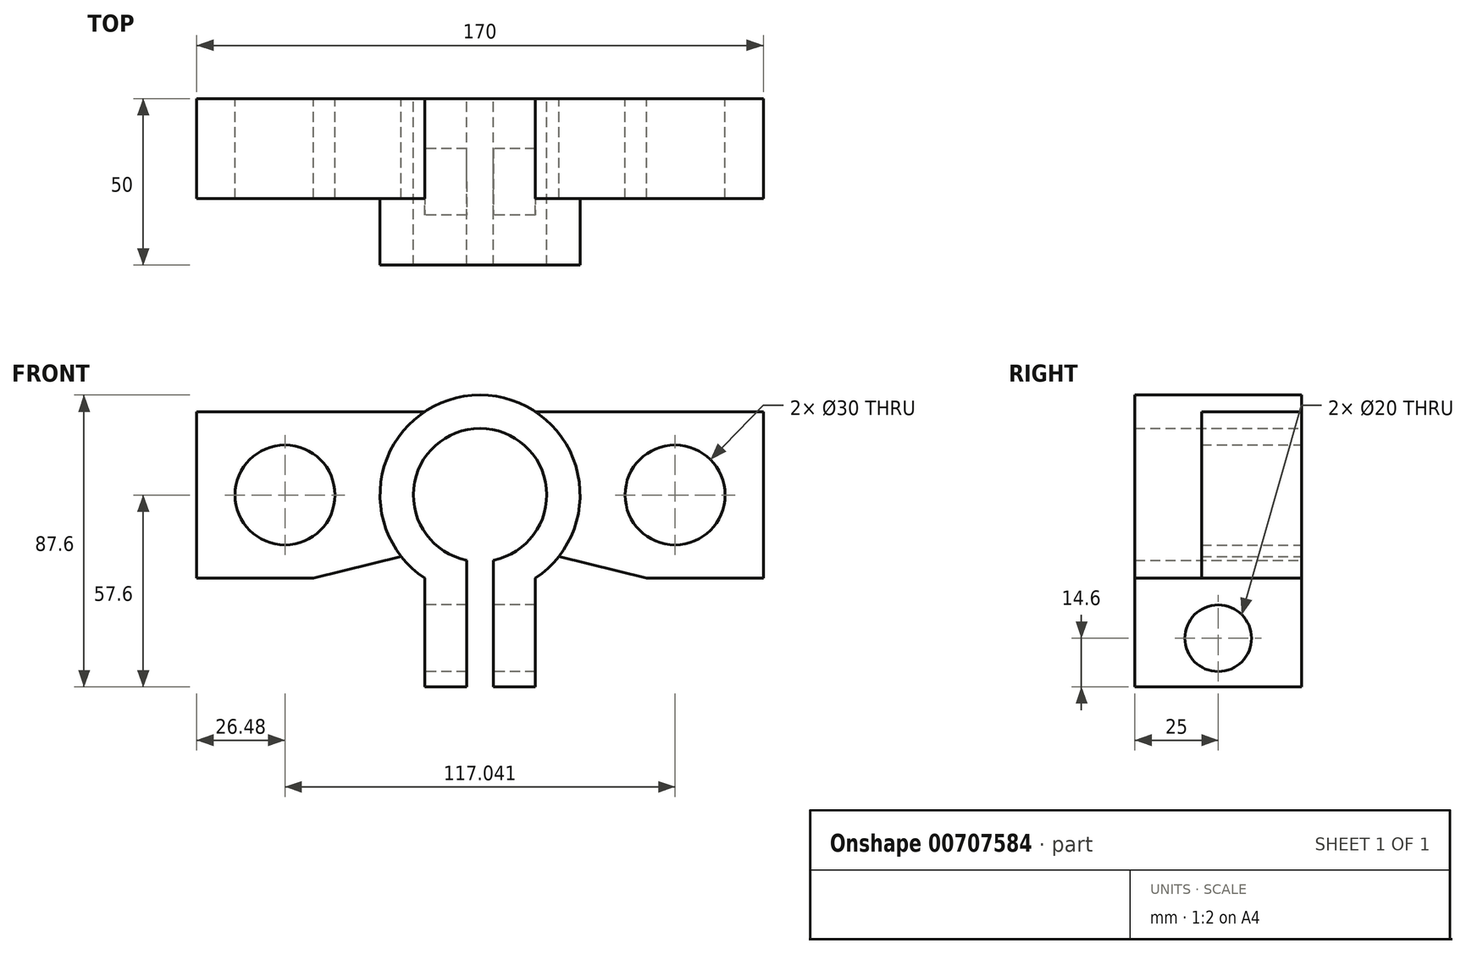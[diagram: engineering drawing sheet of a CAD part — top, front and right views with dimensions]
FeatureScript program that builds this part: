
annotation { "Feature Type Name" : "Feature", "Feature Type Description" : "" }
export const myFeature = defineFeature(function(context is Context, id is Id, definition is map)
    precondition{}
    {
        {
            var Q0;
            Q0=qCreatedBy(makeId("Front.planeOp"),FACE);
            var sketch = newSketch(context, id + "F0", { "sketchPlane" : qUnion([Q0])});
            skCircle(sketch, "E0", {"center": v(0, 0) * mm, "radius": 20 * mm});
            skCircle(sketch, "E1", {"center": v(0, 0) * mm, "radius": 30 * mm});
            skLineSegment(sketch, "E2.bottom", {"start": v(85, -25) * mm, "end": v(-85, -25) * mm});
            skLineSegment(sketch, "E2.top", {"start": v(85, 25) * mm, "end": v(-85, 25) * mm});
            skLineSegment(sketch, "E2.left", {"start": v(85, -25) * mm, "end": v(85, 25) * mm});
            skLineSegment(sketch, "E2.right", {"start": v(-85, -25) * mm, "end": v(-85, 25) * mm});
            skCircle(sketch, "E3", {"center": v(-58.52, 0) * mm, "radius": 15 * mm});
            skCircle(sketch, "E4.MirrorC", {"center": v(58.52, 0) * mm, "radius": 15 * mm});
            skLineSegment(sketch, "E5", {"start": v(-50, -25) * mm, "end": v(-23.65, -18.46) * mm});
            skLineSegment(sketch, "E6.MirrorCS", {"start": v(50, -25) * mm, "end": v(23.65, -18.46) * mm});
            skLineSegment(sketch, "E7", {"start": v(-4, -19.6) * mm, "end": v(-4, -57.6) * mm});
            skLineSegment(sketch, "E8", {"start": v(-16.58, -25) * mm, "end": v(-16.58, -57.6) * mm});
            skLineSegment(sketch, "E9", {"start": v(-4, -57.6) * mm, "end": v(-16.58, -57.6) * mm});
            skPoint(sketch, "E10.orphan", {"position": v(-16.58, -63.2) * mm});
            skLineSegment(sketch, "E11.MirrorCS", {"start": v(4, -19.6) * mm, "end": v(4, -57.6) * mm});
            skLineSegment(sketch, "E12.MirrorCS", {"start": v(16.58, -25) * mm, "end": v(16.58, -57.6) * mm});
            skLineSegment(sketch, "E13.MirrorCS", {"start": v(4, -57.6) * mm, "end": v(16.58, -57.6) * mm});
            skSolve(sketch);
        }
        {
            var Q0;
            {var subQ4=sQuery(id+"F0.wireOp",EDGE,"E7");var subQ5=sQuery(id+"F0.wireOp",EDGE,"E0");var subQ6=makeQuery(id+"F0.imprint","INTERSECT",VERTEX,{"derivedFrom":[subQ5,subQ4]});Q0=makeQuery(id+"F0.imprint","IMPRINT",FACE,{"disambiguationData":[TD([[makeQuery(id+"F0.imprint","IMPRINT",EDGE,{"disambiguationData":[TD([[subQ6,1.0]])],"derivedFrom":subQ5}),-1.0]])]});}
            var Q1;
            {var subQ0=sQuery(id+"F0.wireOp",EDGE,"E2.top");var subQ1=sQuery(id+"F0.wireOp",EDGE,"E1");var subQ2=makeQuery(id+"F0.imprint","INTERSECT",VERTEX,{"disambiguationData":[OD(0.0)],"derivedFrom":[subQ1,subQ0]});Q1=makeQuery(id+"F0.imprint","IMPRINT",FACE,{"disambiguationData":[TD([[makeQuery(id+"F0.imprint","IMPRINT",EDGE,{"disambiguationData":[TD([[subQ2,1.0]])],"derivedFrom":subQ1}),1.0]])]});}
            var Q2;
            {var subQ0=sQuery(id+"F0.wireOp",EDGE,"E12.MirrorCS");Q2=makeQuery(id+"F0.imprint","IMPRINT",FACE,{"disambiguationData":[TD([[makeQuery(id+"F0.imprint","IMPRINT",EDGE,{"derivedFrom":subQ0}),-1.0]])]});}
            var Q3;
            {var subQ1=sQuery(id+"F0.wireOp",EDGE,"E1");var subQ3=sQuery(id+"F0.wireOp",EDGE,"E11.MirrorCS");var subQ4=makeQuery(id+"F0.imprint","INTERSECT",VERTEX,{"derivedFrom":[subQ1,subQ3]});Q3=makeQuery(id+"F0.imprint","IMPRINT",FACE,{"disambiguationData":[TD([[makeQuery(id+"F0.imprint","IMPRINT",EDGE,{"disambiguationData":[TD([[subQ4,1.0]])],"derivedFrom":subQ3}),1.0]])]});}
            var Q4;
            {var subQ0=sQuery(id+"F0.wireOp",EDGE,"E8");Q4=makeQuery(id+"F0.imprint","IMPRINT",FACE,{"disambiguationData":[TD([[makeQuery(id+"F0.imprint","IMPRINT",EDGE,{"derivedFrom":subQ0}),1.0]])]});}
            var Q5;
            {var subQ1=sQuery(id+"F0.wireOp",EDGE,"E1");var subQ3=sQuery(id+"F0.wireOp",EDGE,"E7");var subQ4=makeQuery(id+"F0.imprint","INTERSECT",VERTEX,{"derivedFrom":[subQ1,subQ3]});Q5=makeQuery(id+"F0.imprint","IMPRINT",FACE,{"disambiguationData":[TD([[makeQuery(id+"F0.imprint","IMPRINT",EDGE,{"disambiguationData":[TD([[subQ4,1.0]])],"derivedFrom":subQ3}),-1.0]])]});}
            extrude(context, id + "F1", {"entities" : qUnion([Q0, Q1, Q2, Q3, Q4, Q5]), "depth" : 50 * mm, "offsetDistance" : 25 * mm});
        }
        {
            var Q0;
            {var subQ0=sQuery(id+"F0.wireOp",EDGE,"E2.right");Q0=makeQuery(id+"F0.imprint","IMPRINT",FACE,{"disambiguationData":[TD([[makeQuery(id+"F0.imprint","IMPRINT",EDGE,{"derivedFrom":subQ0}),-1.0]])]});}
            var Q1;
            {var subQ0=sQuery(id+"F0.wireOp",EDGE,"E2.left");Q1=makeQuery(id+"F0.imprint","IMPRINT",FACE,{"disambiguationData":[TD([[makeQuery(id+"F0.imprint","IMPRINT",EDGE,{"derivedFrom":subQ0}),1.0]])]});}
            extrude(context, id + "F2", {"entities" : qUnion([Q0, Q1]), "operationType" : NewBodyOperationType.ADD, "depth" : 30 * mm, "offsetDistance" : 25 * mm});
        }
        {
            var Q0;
            Q0=makeQuery(id+"F1.opExtrude","SWEPT_FACE",FACE,{"disambiguationData":[OSD([sQuery(id+"F0.wireOp",EDGE,"E8")])]});
            var sketch = newSketch(context, id + "F3", { "sketchPlane" : qUnion([Q0])});
            skCircle(sketch, "E14", {"center": v(25, -43) * mm, "radius": 10 * mm});
            skSolve(sketch);
        }
        {
            var Q0;
            Q0=makeQuery(id+"F3.imprint","IMPRINT",FACE,{"disambiguationData":[TD([[makeQuery(id+"F3.imprint","IMPRINT",EDGE,{"derivedFrom":sQuery(id+"F3.wireOp",EDGE,"E14")}),1.0]])]});
            extrude(context, id + "F4", {"entities" : qUnion([Q0]), "operationType" : NewBodyOperationType.REMOVE, "oppositeDirection" : true, "depth" : 42.2 * mm, "offsetDistance" : 25 * mm});
        }
    });
